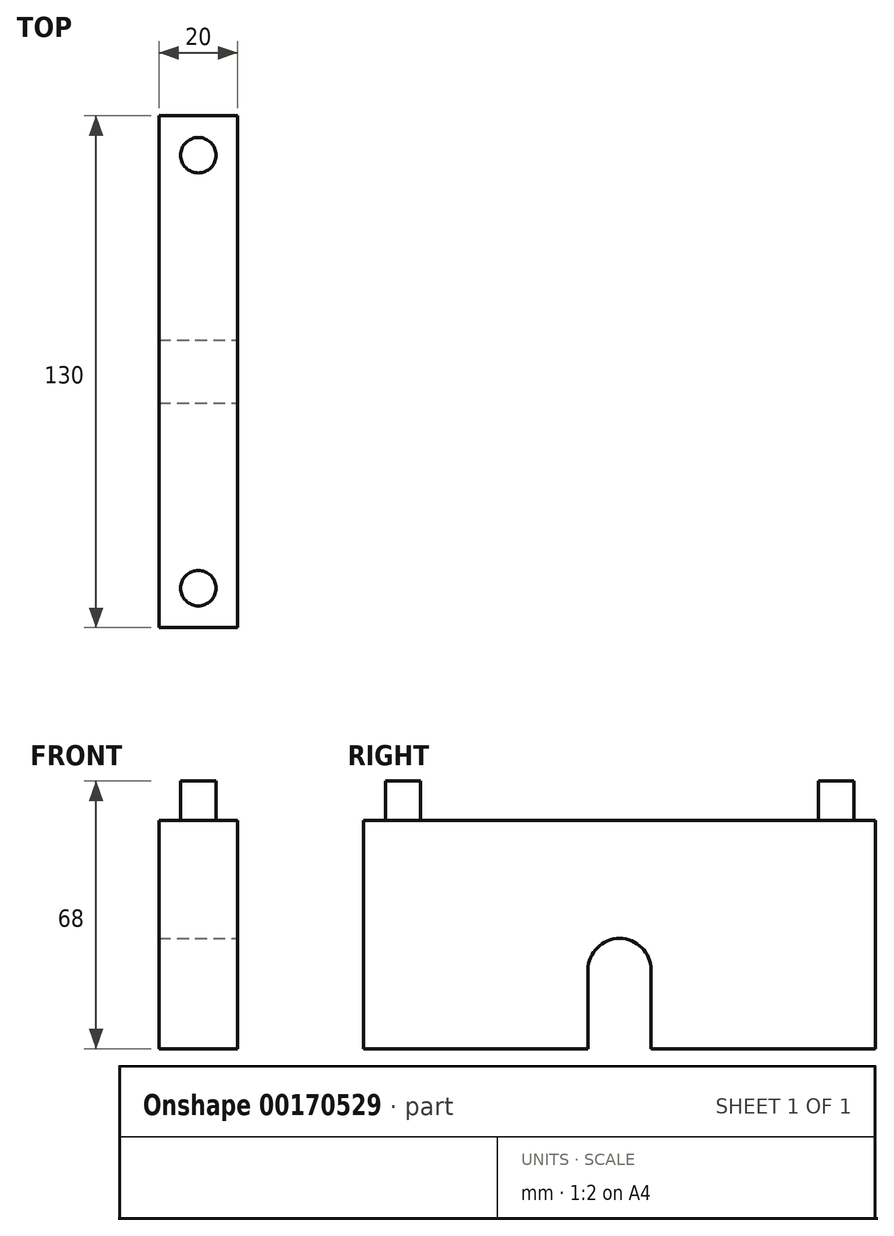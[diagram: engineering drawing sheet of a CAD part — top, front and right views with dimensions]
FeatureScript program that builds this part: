
annotation { "Feature Type Name" : "Feature", "Feature Type Description" : "" }
export const myFeature = defineFeature(function(context is Context, id is Id, definition is map)
    precondition{}
    {
        {
            var Q0;
            Q0=qCreatedBy(makeId("Top.planeOp"),FACE);
            var sketch = newSketch(context, id + "F0", { "sketchPlane" : qUnion([Q0])});
            skLineSegment(sketch, "E0.bottom", {"start": v(0, 0) * mm, "end": v(20, 0) * mm});
            skLineSegment(sketch, "E0.top", {"start": v(0, -130) * mm, "end": v(20, -130) * mm});
            skLineSegment(sketch, "E0.left", {"start": v(0, 0) * mm, "end": v(0, -130) * mm});
            skLineSegment(sketch, "E0.right", {"start": v(20, 0) * mm, "end": v(20, -130) * mm});
            skLineSegment(sketch, "E1", {"start": v(10, 0) * mm, "end": v(10, -130) * mm, "construction": true});
            skSolve(sketch);
        }
        {
            var Q0;
            Q0=makeQuery(id+"F0.imprint","IMPRINT",FACE,{"disambiguationData":[TD([[makeQuery(id+"F0.imprint","IMPRINT",EDGE,{"derivedFrom":sQuery(id+"F0.wireOp",EDGE,"E0.bottom")}),-1.0]])]});
            extrude(context, id + "F1", {"entities" : qUnion([Q0]), "depth" : 58 * mm});
        }
        {
            var Q0;
            Q0=makeQuery(id+"F1.opExtrude","SWEPT_FACE",FACE,{"disambiguationData":[OSD([sQuery(id+"F0.wireOp",EDGE,"E0.right")])]});
            var sketch = newSketch(context, id + "F2", { "sketchPlane" : qUnion([Q0])});
            skLineSegment(sketch, "E2", {"start": v(-65, 40) * mm, "end": v(-65, 0) * mm, "construction": true});
            skArc(sketch, "E3", {"start": v(-57, 20) * mm, "mid": v(-65, 28) * mm, "end": v(-73, 20) * mm});
            skLineSegment(sketch, "E4", {"start": v(-73, 20) * mm, "end": v(-73, 0) * mm});
            skLineSegment(sketch, "E5", {"start": v(-57, 20) * mm, "end": v(-57, 0) * mm});
            skLineSegment(sketch, "E6", {"start": v(-57, 0) * mm, "end": v(-73, 0) * mm});
            skSolve(sketch);
        }
        {
            var Q0;
            Q0=makeQuery(id+"F2.imprint","IMPRINT",FACE,{"disambiguationData":[TD([[makeQuery(id+"F2.imprint","IMPRINT",EDGE,{"derivedFrom":sQuery(id+"F2.wireOp",EDGE,"E3")}),1.0]])]});
            extrude(context, id + "F3", {"entities" : qUnion([Q0]), "operationType" : NewBodyOperationType.REMOVE, "endBound" : BoundingType.THROUGH_ALL, "oppositeDirection" : true, "depth" : 25 * mm});
        }
        {
            var Q0;
            Q0=makeQuery(id+"F1.opExtrude","CAP_FACE",FACE,{"disambiguationData":[OSD([sQuery(id+"F0.wireOp",EDGE,"E0.bottom"),sQuery(id+"F0.wireOp",EDGE,"E0.top"),sQuery(id+"F0.wireOp",EDGE,"E0.left"),sQuery(id+"F0.wireOp",EDGE,"E0.right")])],"isStart":false});
            var sketch = newSketch(context, id + "F4", { "sketchPlane" : qUnion([Q0])});
            skLineSegment(sketch, "E7", {"start": v(10, 0) * mm, "end": v(10, -130) * mm, "construction": true});
            skCircle(sketch, "E8", {"center": v(10, -10) * mm, "radius": 4.5 * mm});
            skCircle(sketch, "E9", {"center": v(10, -120) * mm, "radius": 4.5 * mm});
            skSolve(sketch);
        }
        {
            var Q0;
            Q0=makeQuery(id+"F4.imprint","IMPRINT",FACE,{"disambiguationData":[TD([[makeQuery(id+"F4.imprint","IMPRINT",EDGE,{"derivedFrom":sQuery(id+"F4.wireOp",EDGE,"E8")}),1.0]])]});
            var Q1;
            Q1=makeQuery(id+"F4.imprint","IMPRINT",FACE,{"disambiguationData":[TD([[makeQuery(id+"F4.imprint","IMPRINT",EDGE,{"derivedFrom":sQuery(id+"F4.wireOp",EDGE,"E9")}),1.0]])]});
            extrude(context, id + "F5", {"entities" : qUnion([Q0, Q1]), "operationType" : NewBodyOperationType.ADD, "depth" : 10 * mm});
        }
    });
